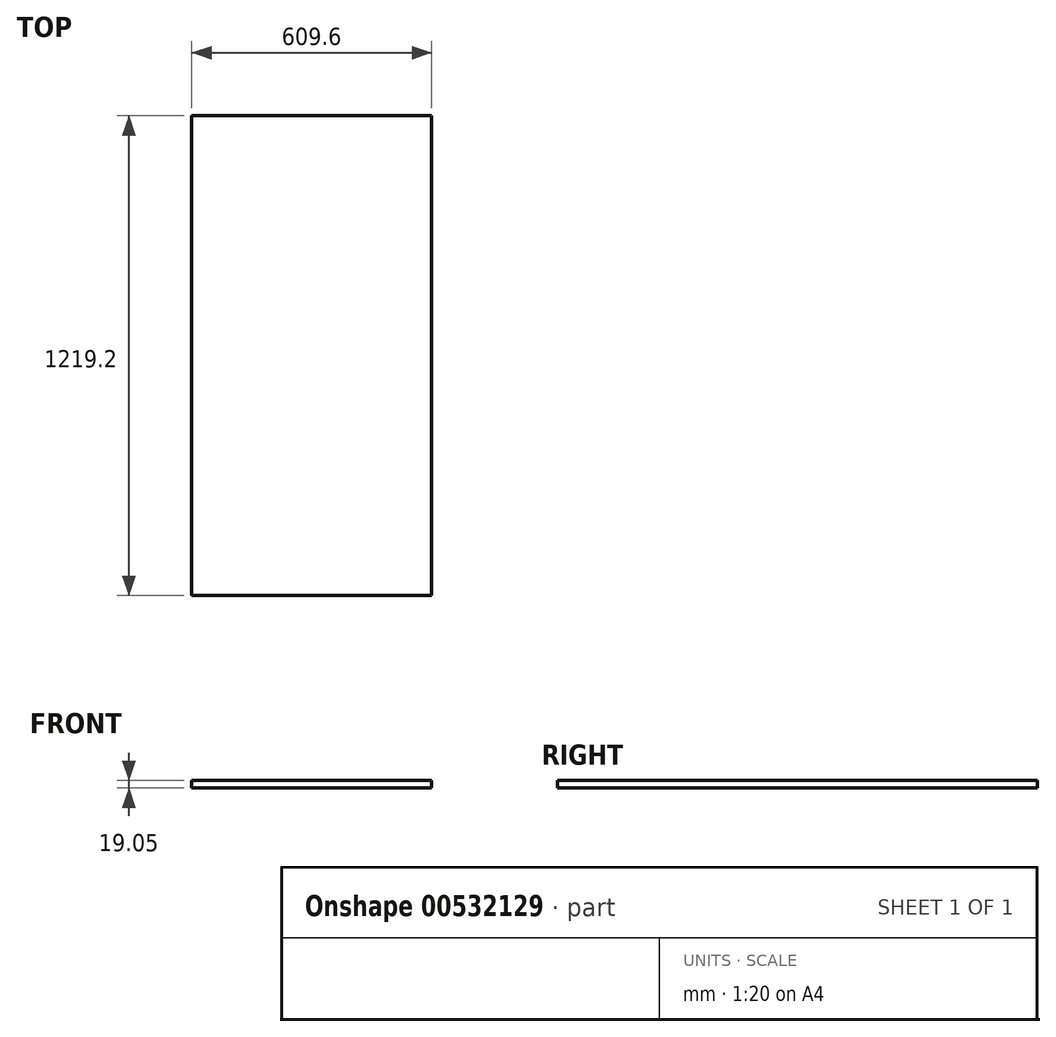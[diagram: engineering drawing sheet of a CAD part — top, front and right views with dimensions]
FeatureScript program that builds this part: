
annotation { "Feature Type Name" : "Feature", "Feature Type Description" : "" }
export const myFeature = defineFeature(function(context is Context, id is Id, definition is map)
    precondition{}
    {
        {
            var Q0;
            Q0=qCreatedBy(makeId("Top.planeOp"),FACE);
            var sketch = newSketch(context, id + "F0", { "sketchPlane" : qUnion([Q0])});
            skLineSegment(sketch, "E0.bottom", {"start": v(304.8, -609.6) * mm, "end": v(-304.8, -609.6) * mm});
            skLineSegment(sketch, "E0.top", {"start": v(304.8, 609.6) * mm, "end": v(-304.8, 609.6) * mm});
            skLineSegment(sketch, "E0.left", {"start": v(304.8, -609.6) * mm, "end": v(304.8, 609.6) * mm});
            skLineSegment(sketch, "E0.right", {"start": v(-304.8, -609.6) * mm, "end": v(-304.8, 609.6) * mm});
            skPoint(sketch, "E0.middle", {"position": v(0, 0) * mm});
            skSolve(sketch);
        }
        {
            var Q0;
            Q0=qSketchRegion(id+"F0",true);
            extrude(context, id + "F1", {"entities" : qUnion([Q0]), "depth" : 19.05 * mm, "offsetDistance" : 25.4 * mm});
        }
    });
